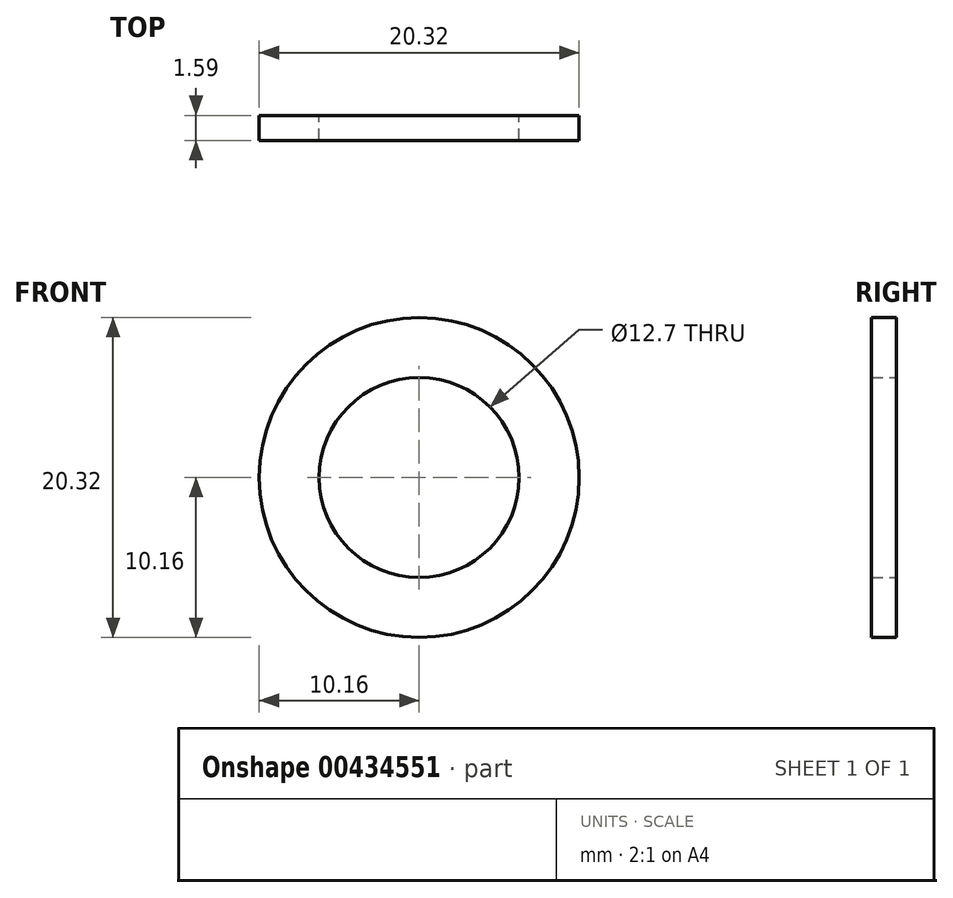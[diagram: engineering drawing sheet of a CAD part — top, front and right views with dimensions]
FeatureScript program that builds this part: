
annotation { "Feature Type Name" : "Feature", "Feature Type Description" : "" }
export const myFeature = defineFeature(function(context is Context, id is Id, definition is map)
    precondition{}
    {
        {
            var Q0;
            Q0=qCreatedBy(makeId("Front.planeOp"),FACE);
            var sketch = newSketch(context, id + "F0", { "sketchPlane" : qUnion([Q0])});
            skCircle(sketch, "E0", {"center": v(0, 0) * mm, "radius": 10.16 * mm});
            skCircle(sketch, "E1", {"center": v(0, 0) * mm, "radius": 6.35 * mm});
            skSolve(sketch);
        }
        {
            var Q0;
            Q0 = qSketchRegion(id + "F0", true);
            extrude(context, id + "F1", {"entities" : qUnion([Q0]), "depth" : 1.59 * mm});
        }
    });
